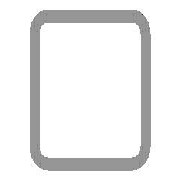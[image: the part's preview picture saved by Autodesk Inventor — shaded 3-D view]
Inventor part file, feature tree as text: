
AUTODESK INVENTOR PART (.ipt)
format: ipt  version: 2025.3 (Build 293356030, 356C)  size: 145,408 bytes
history: native  units: mm (DEFAULTED — no unit token found)
features: other x4, plane x3, split x2, sketch x1
ambient origin geometry x8: Origin, YZ Plane, XZ Plane, XY Plane, X Axis, Y Axis, Z Axis, Center Point
bodies: Solid1 (feature_tree), Body (feature_tree)
feature tree (10):
  parser-record x1  (decoder bookkeeping rows leaked as tree rows — omitted from the tree; the rows remain in map.json)
  other  "Driven Length"
  other  "Start Plane"
  other  "End Plane"
  plane  "Work Plane4"
  split  "Split1"
  plane  "Work Plane5"
  split  "Split2"
  sketch  "Sketch3"  dims[d3=2559.340203mm d4=0.0mm d7=6.0mm d9=80.0mm d11=80.0mm d12=3.0mm d13=80.0mm d14=2639.340203mm d15=40.0mm d16=40.0mm d17=90.0deg d18=2559.340203mm]
  plane  "Work Plane3"
